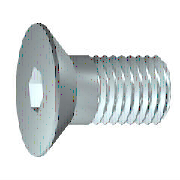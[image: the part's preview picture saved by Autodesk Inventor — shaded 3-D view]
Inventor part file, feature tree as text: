
AUTODESK INVENTOR PART (.ipt)
format: ipt  version: 2020 (Build 240168000, 168)  size: 180,736 bytes
history: native  units: mm (DEFAULTED — no unit token found)
features: sketch x2, extrude x1, plane x1
ambient origin geometry x7: Origin, YZ Plane, XY Plane, X Axis, Y Axis, Z Axis, Center Point
bodies: Solid1 (feature_tree), Body (feature_tree)
feature tree (4):
  sketch  "Sketch2"  dims[d2=1.1mm d3=3.0mm d6=1.86mm d7=45.0deg d8=2.309401mm d9=60.0deg d10=5.54mm d11=3.0mm d12=0.306725mm d13=90.0deg d30=10.0mm d14=0.0mm d15=12.0mm d16=0.0mm d17=0.306725mm d18=0.306725mm d20=0.0mm d39=45.0deg d43=0.0mm d44=0.0mm]
  extrude  "Slot"  Depth=12.0mm
  plane  "Work Plane1"
  sketch  "Sketch1"  dims[d0=16.0mm d1=12.0mm]
